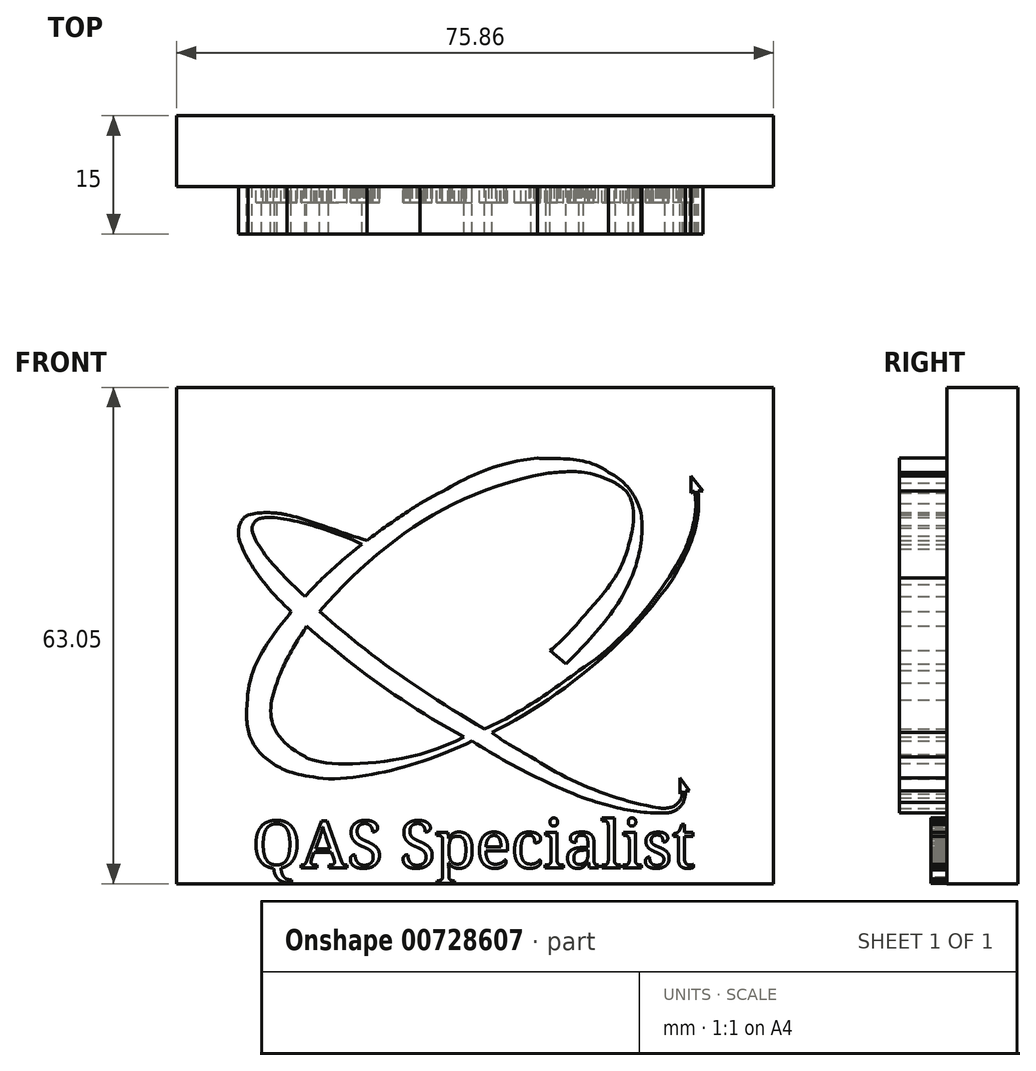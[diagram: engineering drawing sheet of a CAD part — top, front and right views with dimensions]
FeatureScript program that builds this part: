
annotation { "Feature Type Name" : "Feature", "Feature Type Description" : "" }
export const myFeature = defineFeature(function(context is Context, id is Id, definition is map)
    precondition{}
    {
        {
            var Q0;
            Q0=qCreatedBy(makeId("Front.planeOp"),FACE);
            var sketch = newSketch(context, id + "F0", { "sketchPlane" : qUnion([Q0])});
            skFitSpline(sketch, "E0", {"points": [v(-20.5, 30.87) * mm, v(-13.75, 31.7) * mm], "startDerivative": vector(1.32, -1.32) * mm, "endDerivative": vector(8.3, 4.33) * mm});
            skFitSpline(sketch, "E1", {"points": [v(-20.5, 30.87) * mm, v(-21.68, 33.98) * mm], "startDerivative": vector(-4.95, 2.56) * mm, "endDerivative": vector(1.32, 3.47) * mm});
            skFitSpline(sketch, "E2", {"points": [v(-21.68, 33.98) * mm, v(-20.4, 36.39) * mm], "startDerivative": vector(0.54, 1.88) * mm, "endDerivative": vector(1.39, 2.01) * mm});
            skFitSpline(sketch, "E3", {"points": [v(-20.4, 36.39) * mm, v(-13.75, 31.7) * mm], "startDerivative": vector(5.07, -4.51) * mm, "endDerivative": vector(7.95, -4.26) * mm});
            skFitSpline(sketch, "E4", {"points": [v(-19.86, 37.02) * mm, v(-12.88, 32.03) * mm], "startDerivative": vector(5.93, -5.4) * mm, "endDerivative": vector(7.95, -4.6) * mm});
            skFitSpline(sketch, "E5", {"points": [v(-19.86, 37.02) * mm, v(-10.29, 42.86) * mm], "startDerivative": vector(7.55, 8.6) * mm, "endDerivative": vector(12.42, 2.4) * mm});
            skFitSpline(sketch, "E6", {"points": [v(-10.29, 42.86) * mm, v(-7.34, 42.44) * mm], "startDerivative": vector(2.78, 0.17) * mm, "endDerivative": vector(3.94, -2.01) * mm});
            skFitSpline(sketch, "E7", {"points": [v(-7.34, 42.44) * mm, v(-6.59, 40.65) * mm], "startDerivative": vector(0.83, -0.6) * mm, "endDerivative": vector(-0.4, -4.15) * mm});
            skFitSpline(sketch, "E8", {"points": [v(-6.59, 40.65) * mm, v(-8.22, 37.33) * mm], "startDerivative": vector(-0.7, -3.36) * mm, "endDerivative": vector(-3.68, -4.03) * mm});
            skFitSpline(sketch, "E9", {"points": [v(-8.22, 37.33) * mm, v(-10.11, 35.35) * mm], "startDerivative": vector(-1.85, -2.06) * mm, "endDerivative": vector(-2.27, -1.84) * mm});
            skLineSegment(sketch, "E10", {"start": v(-10.11, 35.35) * mm, "end": v(-9.42, 34.8) * mm});
            skFitSpline(sketch, "E11", {"points": [v(-9.42, 34.8) * mm, v(-6.8, 38.15) * mm], "startDerivative": vector(2.74, 2.74) * mm, "endDerivative": vector(1.66, 3.68) * mm});
            skFitSpline(sketch, "E12", {"points": [v(-6.8, 38.15) * mm, v(-6.26, 41.17) * mm], "startDerivative": vector(1.43, 2.79) * mm, "endDerivative": vector(-0.44, 2.56) * mm});
            skFitSpline(sketch, "E13", {"points": [v(-6.26, 41.17) * mm, v(-7.63, 42.9) * mm], "startDerivative": vector(-0.41, 1.98) * mm, "endDerivative": vector(-2.08, 0.88) * mm});
            skFitSpline(sketch, "E14", {"points": [v(-7.63, 42.9) * mm, v(-10.64, 43.5) * mm], "startDerivative": vector(-3.03, 2.2) * mm, "endDerivative": vector(-2.58, 0.19) * mm});
            skFitSpline(sketch, "E15", {"points": [v(-10.64, 43.5) * mm, v(-15.62, 41.58) * mm], "startDerivative": vector(-7.01, -0.7) * mm, "endDerivative": vector(-4.62, -2.36) * mm});
            skFitSpline(sketch, "E16", {"points": [v(-15.62, 41.58) * mm, v(-20.48, 37.65) * mm], "startDerivative": vector(-3.7, -2.4) * mm, "endDerivative": vector(-4.44, -5.02) * mm});
            skFitSpline(sketch, "E17", {"points": [v(-20.48, 37.65) * mm, v(-22.73, 40.54) * mm], "startDerivative": vector(-3.34, 2.9) * mm, "endDerivative": vector(-0.07, 1.98) * mm});
            skFitSpline(sketch, "E18", {"points": [v(-22.73, 40.54) * mm, v(-21.77, 40.98) * mm], "startDerivative": vector(0.28, 0.94) * mm, "endDerivative": vector(2.33, -0.14) * mm});
            skFitSpline(sketch, "E19", {"points": [v(-21.77, 40.98) * mm, v(-18.07, 39.86) * mm], "startDerivative": vector(2.7, -0.31) * mm, "endDerivative": vector(3.96, -1.9) * mm});
            skFitSpline(sketch, "E20", {"points": [v(-17.87, 40.01) * mm, v(-21.24, 41.1) * mm], "startDerivative": vector(-4.56, 1.43) * mm, "endDerivative": vector(-3.06, 0.68) * mm});
            skFitSpline(sketch, "E21", {"points": [v(-21.24, 41.1) * mm, v(-22.9, 41.1) * mm], "startDerivative": vector(-0.74, 0.14) * mm, "endDerivative": vector(-2.37, -0.56) * mm});
            skFitSpline(sketch, "E22", {"points": [v(-22.9, 41.1) * mm, v(-23.3, 40.2) * mm], "startDerivative": vector(-0.52, -0.3) * mm, "endDerivative": vector(0.06, -1.94) * mm});
            skFitSpline(sketch, "E23", {"points": [v(-23.3, 40.2) * mm, v(-21.07, 37) * mm], "startDerivative": vector(0.68, -2.9) * mm, "endDerivative": vector(3.23, -2.98) * mm});
            skFitSpline(sketch, "E24", {"points": [v(-21.07, 37) * mm, v(-22.93, 33.27) * mm], "startDerivative": vector(-2.17, -2.97) * mm, "endDerivative": vector(-0.3, -5.14) * mm});
            skFitSpline(sketch, "E25", {"points": [v(-22.93, 33.27) * mm, v(-22.32, 30.95) * mm], "startDerivative": vector(-0.26, -3.01) * mm, "endDerivative": vector(1.87, -2.01) * mm});
            skFitSpline(sketch, "E26", {"points": [v(-22.32, 30.95) * mm, v(-19.5, 29.92) * mm], "startDerivative": vector(2.11, -1.77) * mm, "endDerivative": vector(5.3, -0.54) * mm});
            skFitSpline(sketch, "E27", {"points": [v(-19.5, 29.92) * mm, v(-13.4, 31.53) * mm], "startDerivative": vector(5.84, 0.05) * mm, "endDerivative": vector(5.6, 2.7) * mm});
            skFitSpline(sketch, "E28", {"points": [v(-13.4, 31.53) * mm, v(-8.68, 29.12) * mm], "startDerivative": vector(4.12, -2.67) * mm, "endDerivative": vector(5.37, -2.1) * mm});
            skFitSpline(sketch, "E29", {"points": [v(-8.68, 29.12) * mm, v(-5.25, 28.48) * mm], "startDerivative": vector(4.09, -1.34) * mm, "endDerivative": vector(3.62, 0.12) * mm});
            skFitSpline(sketch, "E30", {"points": [v(-5.25, 28.48) * mm, v(-4.47, 28.92) * mm], "startDerivative": vector(0.86, -0.07) * mm, "endDerivative": vector(0.52, 0.93) * mm});
            skFitSpline(sketch, "E31", {"points": [v(-4.47, 28.92) * mm, v(-4.37, 29.4) * mm], "startDerivative": vector(0.2, 0.42) * mm, "endDerivative": vector(0, 0.47) * mm});
            skLineSegment(sketch, "E32", {"start": v(-4.37, 29.4) * mm, "end": v(-4.21, 29.4) * mm});
            skLineSegment(sketch, "E33", {"start": v(-4.21, 29.4) * mm, "end": v(-4.6, 29.96) * mm});
            skLineSegment(sketch, "E34", {"start": v(-4.6, 29.96) * mm, "end": v(-4.6, 29.3) * mm});
            skLineSegment(sketch, "E35", {"start": v(-4.6, 29.3) * mm, "end": v(-4.5, 29.4) * mm});
            skFitSpline(sketch, "E36", {"points": [v(-4.5, 29.4) * mm, v(-5.52, 28.7) * mm], "startDerivative": vector(-0.12, -1.94) * mm, "endDerivative": vector(-1.42, 0.25) * mm});
            skFitSpline(sketch, "E37", {"points": [v(-5.52, 28.7) * mm, v(-10.9, 30.85) * mm], "startDerivative": vector(-5.78, 0.96) * mm, "endDerivative": vector(-4.49, 3.01) * mm});
            skFitSpline(sketch, "E38", {"points": [v(-10.9, 30.85) * mm, v(-12.57, 31.88) * mm], "startDerivative": vector(-1.92, 1.07) * mm, "endDerivative": vector(-1.41, 1.12) * mm});
            skFitSpline(sketch, "E39", {"points": [v(-12.57, 31.88) * mm, v(-4.88, 38.43) * mm], "startDerivative": vector(7.56, 3.84) * mm, "endDerivative": vector(6.6, 9.46) * mm});
            skFitSpline(sketch, "E40", {"points": [v(-4.88, 38.43) * mm, v(-3.85, 42.1) * mm], "startDerivative": vector(2, 3.63) * mm, "endDerivative": vector(-0.5, 3.95) * mm});
            skLineSegment(sketch, "E41", {"start": v(-3.85, 42.1) * mm, "end": v(-3.64, 42.1) * mm});
            skLineSegment(sketch, "E42", {"start": v(-3.64, 42.1) * mm, "end": v(-4.14, 42.74) * mm});
            skLineSegment(sketch, "E43", {"start": v(-4.14, 42.74) * mm, "end": v(-4.14, 42.03) * mm});
            skLineSegment(sketch, "E44", {"start": v(-4.14, 42.03) * mm, "end": v(-4, 42.1) * mm});
            skFitSpline(sketch, "E45", {"points": [v(-4, 42.1) * mm, v(-4.38, 39.65) * mm], "startDerivative": vector(0.54, -2.69) * mm, "endDerivative": vector(-0.84, -2.17) * mm});
            skFitSpline(sketch, "E46", {"points": [v(-4.38, 39.65) * mm, v(-8.88, 34.5) * mm], "startDerivative": vector(-2.48, -5.04) * mm, "endDerivative": vector(-5.41, -3.24) * mm});
            skFitSpline(sketch, "E47", {"points": [v(-8.88, 34.5) * mm, v(-12.88, 32.03) * mm], "startDerivative": vector(-3.7, -2.8) * mm, "endDerivative": vector(-4.16, -1.78) * mm});
            skSolve(sketch);
        }
        {
            var Q0;
            Q0 = qSketchRegion(id + "F0", true);
            extrude(context, id + "F1", {"entities" : qUnion([Q0]), "depth" : 5 * mm, "offsetDistance" : 25 * mm});
        }
        {
            var Q0;
            Q0=qCreatedBy(makeId("Front.planeOp"),FACE);
            var sketch = newSketch(context, id + "F2", { "sketchPlane" : qUnion([Q0])});
            skLineSegment(sketch, "E48.bottom", {"start": v(-25.93, 46.5) * mm, "end": v(-0.64, 46.5) * mm});
            skLineSegment(sketch, "E48.top", {"start": v(-25.93, 25.48) * mm, "end": v(-0.64, 25.48) * mm});
            skLineSegment(sketch, "E48.left", {"start": v(-25.93, 46.5) * mm, "end": v(-25.93, 25.48) * mm});
            skLineSegment(sketch, "E48.right", {"start": v(-0.64, 46.5) * mm, "end": v(-0.64, 25.48) * mm});
            skSolve(sketch);
        }
        {
            var Q0;
            Q0=makeQuery(id+"F2.imprint","IMPRINT",FACE,{"disambiguationData":[TD([[makeQuery(id+"F2.imprint","IMPRINT",EDGE,{"derivedFrom":sQuery(id+"F2.wireOp",EDGE,"E48.bottom")}),-1.0]])]});
            extrude(context, id + "F3", {"entities" : qUnion([Q0]), "operationType" : NewBodyOperationType.ADD, "depth" : 3 * mm, "offsetDistance" : 25 * mm});
        }
        {
            var Q0;
            Q0=makeQuery(id+"F1.opExtrude","SWEPT_BODY",BODY,{"disambiguationData":[OSD([sQuery(id+"F0.wireOp",EDGE,"E0"),sQuery(id+"F0.wireOp",EDGE,"E1"),sQuery(id+"F0.wireOp",EDGE,"E2"),sQuery(id+"F0.wireOp",EDGE,"E3"),sQuery(id+"F0.wireOp",EDGE,"E4"),sQuery(id+"F0.wireOp",EDGE,"E5"),sQuery(id+"F0.wireOp",EDGE,"E6"),sQuery(id+"F0.wireOp",EDGE,"E7"),sQuery(id+"F0.wireOp",EDGE,"E8"),sQuery(id+"F0.wireOp",EDGE,"E9"),sQuery(id+"F0.wireOp",EDGE,"E10"),sQuery(id+"F0.wireOp",EDGE,"E11"),sQuery(id+"F0.wireOp",EDGE,"E12"),sQuery(id+"F0.wireOp",EDGE,"E13"),sQuery(id+"F0.wireOp",EDGE,"E14"),sQuery(id+"F0.wireOp",EDGE,"E15"),sQuery(id+"F0.wireOp",EDGE,"E16"),sQuery(id+"F0.wireOp",EDGE,"E17"),sQuery(id+"F0.wireOp",EDGE,"E18"),sQuery(id+"F0.wireOp",EDGE,"E19"),sQuery(id+"F0.wireOp",EDGE,"E20"),sQuery(id+"F0.wireOp",EDGE,"E21"),sQuery(id+"F0.wireOp",EDGE,"E22"),sQuery(id+"F0.wireOp",EDGE,"E23"),sQuery(id+"F0.wireOp",EDGE,"E24"),sQuery(id+"F0.wireOp",EDGE,"E25"),sQuery(id+"F0.wireOp",EDGE,"E26"),sQuery(id+"F0.wireOp",EDGE,"E27"),sQuery(id+"F0.wireOp",EDGE,"E28"),sQuery(id+"F0.wireOp",EDGE,"E29"),sQuery(id+"F0.wireOp",EDGE,"E30"),sQuery(id+"F0.wireOp",EDGE,"E31"),sQuery(id+"F0.wireOp",EDGE,"E32"),sQuery(id+"F0.wireOp",EDGE,"E33"),sQuery(id+"F0.wireOp",EDGE,"E34"),sQuery(id+"F0.wireOp",EDGE,"E35"),sQuery(id+"F0.wireOp",EDGE,"E36"),sQuery(id+"F0.wireOp",EDGE,"E37"),sQuery(id+"F0.wireOp",EDGE,"E38"),sQuery(id+"F0.wireOp",EDGE,"E39"),sQuery(id+"F0.wireOp",EDGE,"E40"),sQuery(id+"F0.wireOp",EDGE,"E41"),sQuery(id+"F0.wireOp",EDGE,"E42"),sQuery(id+"F0.wireOp",EDGE,"E43"),sQuery(id+"F0.wireOp",EDGE,"E44"),sQuery(id+"F0.wireOp",EDGE,"E45"),sQuery(id+"F0.wireOp",EDGE,"E46"),sQuery(id+"F0.wireOp",EDGE,"E47")])]});
            var Q1;
            Q1=makeQuery(id+"F3.opExtrude","CAP_VERTEX",VERTEX,{"disambiguationData":[OSD([sQuery(id+"F2.wireOp",EDGE,"E48.top"),sQuery(id+"F2.wireOp",EDGE,"E48.right")])],"isStart":false});
            transform(context, id + "F4", {"entities" : qUnion([Q0]), "transformType" : TransformType.SCALE_UNIFORMLY, "scale" : 3, "scalePoint" : qUnion([Q1]), "makeCopy" : false});
        }
        {
            var Q0;
            {var subQ0=sQuery(id+"F2.wireOp",EDGE,"E48.bottom");var subQ4=sQuery(id+"F2.wireOp",EDGE,"E48.top");var subQ5=sQuery(id+"F2.wireOp",EDGE,"E48.left");var subQ6=sQuery(id+"F2.wireOp",EDGE,"E48.right");Q0=makeQuery(id+"F3.boolean.opBoolean","SPLIT",FACE,{"disambiguationData":[TD([makeQuery(id+"F1.opExtrude","SWEPT_FACE",FACE,{"disambiguationData":[OSD([sQuery(id+"F0.wireOp",EDGE,"E4")])]})])],"derivedFrom":makeQuery(id+"F3.opExtrude","CAP_FACE",FACE,{"disambiguationData":[OSD([subQ0,subQ4,subQ5,subQ6])],"isStart":false})});}
            var sketch = newSketch(context, id + "F5", { "sketchPlane" : qUnion([Q0])});
            skText(sketch, "E49", { "text": "QAS Specialist", "fontName": "NotoSerif-Regular.ttf"});
            skLineSegment(sketch, "E50", {"start": v(-38.57, 88.53) * mm, "end": v(-38.57, 12.37) * mm, "construction": true});
            const initialGuessF5  = {"E49": [-0.06688, 0.0275, 1, 0, 0.006]};
            skSetInitialGuess(sketch, initialGuessF5);
            skSolve(sketch);
        }
        {
            var Q0;
            Q0 = qSketchRegion(id + "F5", true);
            extrude(context, id + "F6", {"entities" : qUnion([Q0]), "operationType" : NewBodyOperationType.ADD, "depth" : 2 * mm, "offsetDistance" : 25 * mm});
        }
    });
